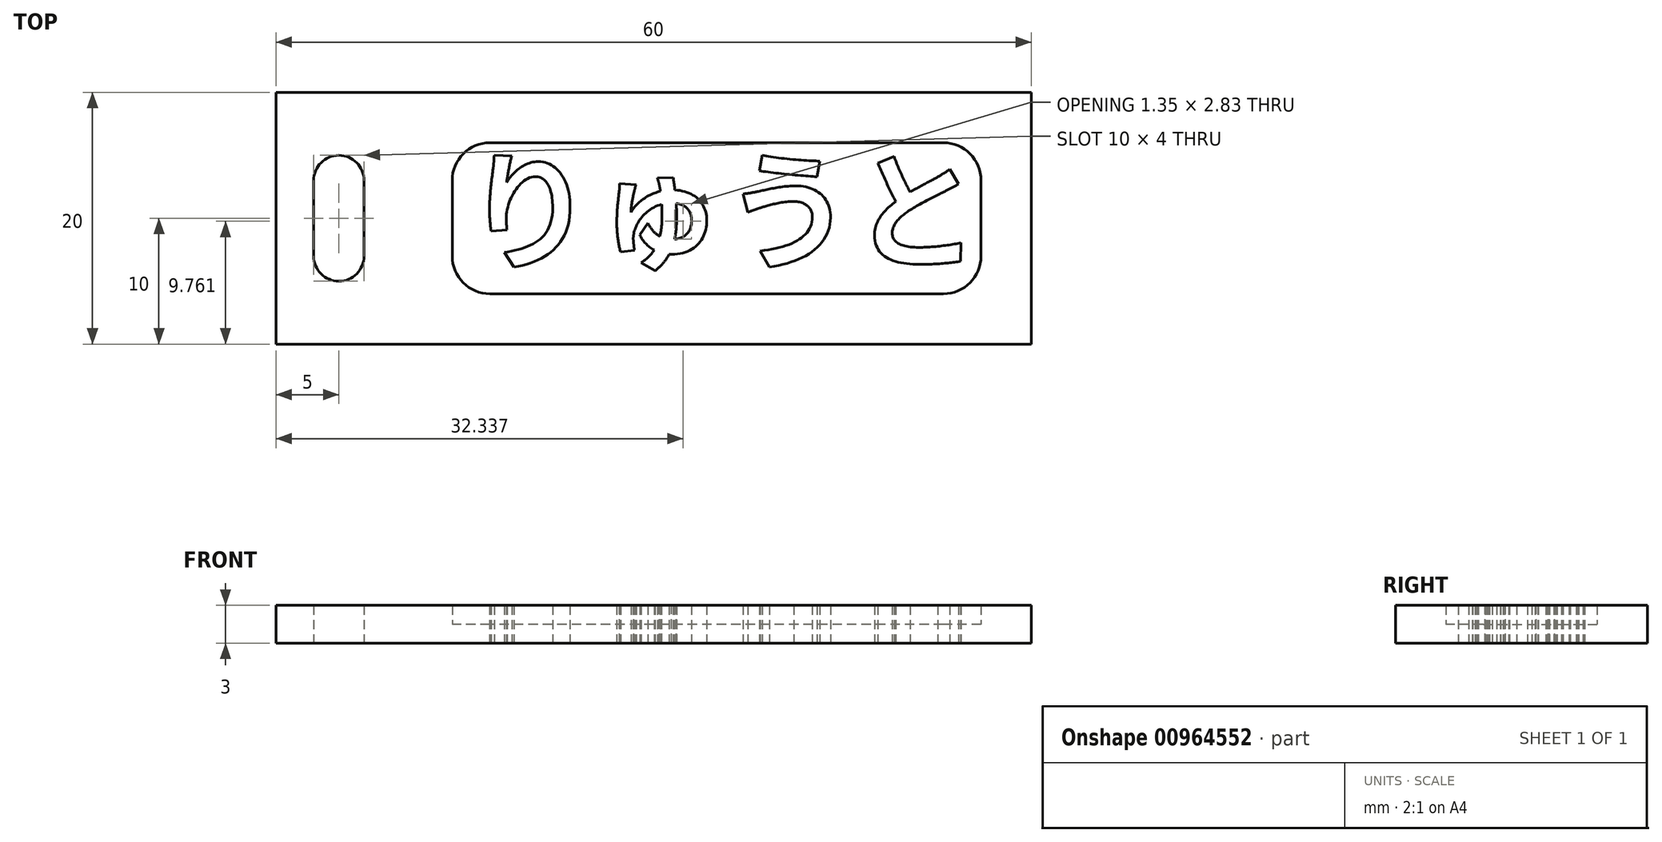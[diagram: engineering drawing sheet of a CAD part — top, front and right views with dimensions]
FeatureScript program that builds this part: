
annotation { "Feature Type Name" : "Feature", "Feature Type Description" : "" }
export const myFeature = defineFeature(function(context is Context, id is Id, definition is map)
    precondition{}
    {
        {
            var Q0;
            Q0=qCreatedBy(makeId("Top.planeOp"),FACE);
            var sketch = newSketch(context, id + "F0", { "sketchPlane" : qUnion([Q0])});
            skLineSegment(sketch, "E0.bottom", {"start": v(25, -10) * mm, "end": v(-25, -10) * mm});
            skLineSegment(sketch, "E0.top", {"start": v(25, 10) * mm, "end": v(-25, 10) * mm});
            skLineSegment(sketch, "E0.left", {"start": v(25, -10) * mm, "end": v(25, 10) * mm});
            skLineSegment(sketch, "E0.right", {"start": v(-25, -10) * mm, "end": v(-25, 10) * mm});
            skPoint(sketch, "E0.middle", {"position": v(0, 0) * mm});
            skLineSegment(sketch, "E1.bottom", {"start": v(-25, 10) * mm, "end": v(-35, 10) * mm});
            skLineSegment(sketch, "E1.top", {"start": v(-25, -10) * mm, "end": v(-35, -10) * mm});
            skLineSegment(sketch, "E1.left", {"start": v(-25, 10) * mm, "end": v(-25, -10) * mm});
            skLineSegment(sketch, "E1.right", {"start": v(-35, 10) * mm, "end": v(-35, -10) * mm});
            skPoint(sketch, "E1.middle", {"position": v(-30, 0) * mm});
            skLineSegment(sketch, "E2.bottom", {"start": v(-30, -5) * mm, "end": v(-30, -5) * mm});
            skLineSegment(sketch, "E2.top", {"start": v(-30, 5) * mm, "end": v(-30, 5) * mm});
            skLineSegment(sketch, "E2.left", {"start": v(-28, -3) * mm, "end": v(-28, 3) * mm});
            skLineSegment(sketch, "E2.right", {"start": v(-32, -3) * mm, "end": v(-32, 3) * mm});
            skPoint(sketch, "E3.visualSharp", {"position": v(-32, 5) * mm});
            skArc(sketch, "E3.filletArc", {"start": v(-30, 5) * mm, "mid": v(-31.41, 4.41) * mm, "end": v(-32, 3) * mm});
            skPoint(sketch, "E4.visualSharp", {"position": v(-28, -5) * mm});
            skArc(sketch, "E4.filletArc", {"start": v(-30, -5) * mm, "mid": v(-28.59, -4.41) * mm, "end": v(-28, -3) * mm});
            skPoint(sketch, "E5.visualSharp", {"position": v(-32, -5) * mm});
            skArc(sketch, "E5.filletArc", {"start": v(-32, -3) * mm, "mid": v(-31.41, -4.41) * mm, "end": v(-30, -5) * mm});
            skPoint(sketch, "E6.visualSharp", {"position": v(-28, 5) * mm});
            skArc(sketch, "E6.filletArc", {"start": v(-28, 3) * mm, "mid": v(-28.59, 4.41) * mm, "end": v(-30, 5) * mm});
            skSolve(sketch);
        }
        {
            var Q0;
            Q0 = qSketchRegion(id + "F0", true);
            extrude(context, id + "F1", {"entities" : qUnion([Q0]), "depth" : 3 * mm, "offsetDistance" : 25 * mm});
        }
        {
            var Q0;
            Q0=qCreatedBy(makeId("Top.planeOp"),FACE);
            var sketch = newSketch(context, id + "F2", { "sketchPlane" : qUnion([Q0])});
            skLineSegment(sketch, "E7.bottom", {"start": v(18, -6) * mm, "end": v(-18, -6) * mm});
            skLineSegment(sketch, "E7.top", {"start": v(18, 6) * mm, "end": v(-18, 6) * mm});
            skLineSegment(sketch, "E7.left", {"start": v(21, -3) * mm, "end": v(21, 3) * mm});
            skLineSegment(sketch, "E7.right", {"start": v(-21, -3) * mm, "end": v(-21, 3) * mm});
            skPoint(sketch, "E7.middle", {"position": v(0, 0) * mm});
            skPoint(sketch, "E8.visualSharp", {"position": v(-21, 6) * mm});
            skArc(sketch, "E8.filletArc", {"start": v(-18, 6) * mm, "mid": v(-20.12, 5.12) * mm, "end": v(-21, 3) * mm});
            skPoint(sketch, "E9.visualSharp", {"position": v(21, 6) * mm});
            skArc(sketch, "E9.filletArc", {"start": v(21, 3) * mm, "mid": v(20.12, 5.12) * mm, "end": v(18, 6) * mm});
            skPoint(sketch, "E10.visualSharp", {"position": v(21, -6) * mm});
            skArc(sketch, "E10.filletArc", {"start": v(18, -6) * mm, "mid": v(20.12, -5.12) * mm, "end": v(21, -3) * mm});
            skPoint(sketch, "E11.visualSharp", {"position": v(-21, -6) * mm});
            skArc(sketch, "E11.filletArc", {"start": v(-21, -3) * mm, "mid": v(-20.12, -5.12) * mm, "end": v(-18, -6) * mm});
            skSolve(sketch);
        }
        {
            var Q0;
            Q0 = qSketchRegion(id + "F2", true);
            extrude(context, id + "F3", {"entities" : qUnion([Q0]), "depth" : 3 * mm, "offsetDistance" : 25 * mm});
        }
        {
            var Q0;
            Q0=makeQuery(id+"F3.opExtrude","SWEPT_BODY",BODY,{"disambiguationData":[OSD([sQuery(id+"F2.wireOp",EDGE,"E7.bottom"),sQuery(id+"F2.wireOp",EDGE,"E7.top"),sQuery(id+"F2.wireOp",EDGE,"E7.left"),sQuery(id+"F2.wireOp",EDGE,"E7.right"),sQuery(id+"F2.wireOp",EDGE,"E8.filletArc"),sQuery(id+"F2.wireOp",EDGE,"E9.filletArc"),sQuery(id+"F2.wireOp",EDGE,"E10.filletArc"),sQuery(id+"F2.wireOp",EDGE,"E11.filletArc")])]});
            transform(context, id + "F4", {"entities" : qUnion([Q0]), "transformType" : TransformType.TRANSLATION_3D, "dx" : 0 * mm, "dy" : 0 * mm, "dz" : 1.5 * mm, "makeCopy" : false});
        }
        {
            var Q0;
            Q0=makeQuery(id+"F3.opExtrude","SWEPT_BODY",BODY,{"disambiguationData":[OSD([sQuery(id+"F2.wireOp",EDGE,"E7.bottom"),sQuery(id+"F2.wireOp",EDGE,"E7.top"),sQuery(id+"F2.wireOp",EDGE,"E7.left"),sQuery(id+"F2.wireOp",EDGE,"E7.right"),sQuery(id+"F2.wireOp",EDGE,"E8.filletArc"),sQuery(id+"F2.wireOp",EDGE,"E9.filletArc"),sQuery(id+"F2.wireOp",EDGE,"E10.filletArc"),sQuery(id+"F2.wireOp",EDGE,"E11.filletArc")])]});
            var Q1;
            Q1=makeQuery(id+"F1.opExtrude","SWEPT_BODY",BODY,{"disambiguationData":[OSD([sQuery(id+"F0.wireOp",EDGE,"E0.bottom"),sQuery(id+"F0.wireOp",EDGE,"E0.top"),sQuery(id+"F0.wireOp",EDGE,"E0.left"),sQuery(id+"F0.wireOp",EDGE,"E1.bottom"),sQuery(id+"F0.wireOp",EDGE,"E1.top"),sQuery(id+"F0.wireOp",EDGE,"E1.right"),sQuery(id+"F0.wireOp",EDGE,"E2.left"),sQuery(id+"F0.wireOp",EDGE,"E2.right"),sQuery(id+"F0.wireOp",EDGE,"E3.filletArc"),sQuery(id+"F0.wireOp",EDGE,"E4.filletArc"),sQuery(id+"F0.wireOp",EDGE,"E5.filletArc"),sQuery(id+"F0.wireOp",EDGE,"E6.filletArc")])]});
            booleanBodies(context, id + "F5", {"operationType" : BooleanOperationType.SUBTRACTION, "tools" : qUnion([Q0]), "targets" : qUnion([Q1])});
        }
        {
            var Q0;
            Q0=qCreatedBy(makeId("Top.planeOp"),FACE);
            var sketch = newSketch(context, id + "F6", { "sketchPlane" : qUnion([Q0])});
            skText(sketch, "E12", { "text": "りゅうと", "fontName": "NotoSansCJKjp-Bold.otf"});
            const initialGuessF6  = {"E12": [-0.02, -0.00327, 1, 0, 0.00741]};
            skSetInitialGuess(sketch, initialGuessF6);
            skSolve(sketch);
        }
        {
            var Q0;
            Q0 = qSketchRegion(id + "F6", true);
            extrude(context, id + "F7", {"entities" : qUnion([Q0]), "depth" : 3 * mm, "offsetDistance" : 25 * mm});
        }
    });
